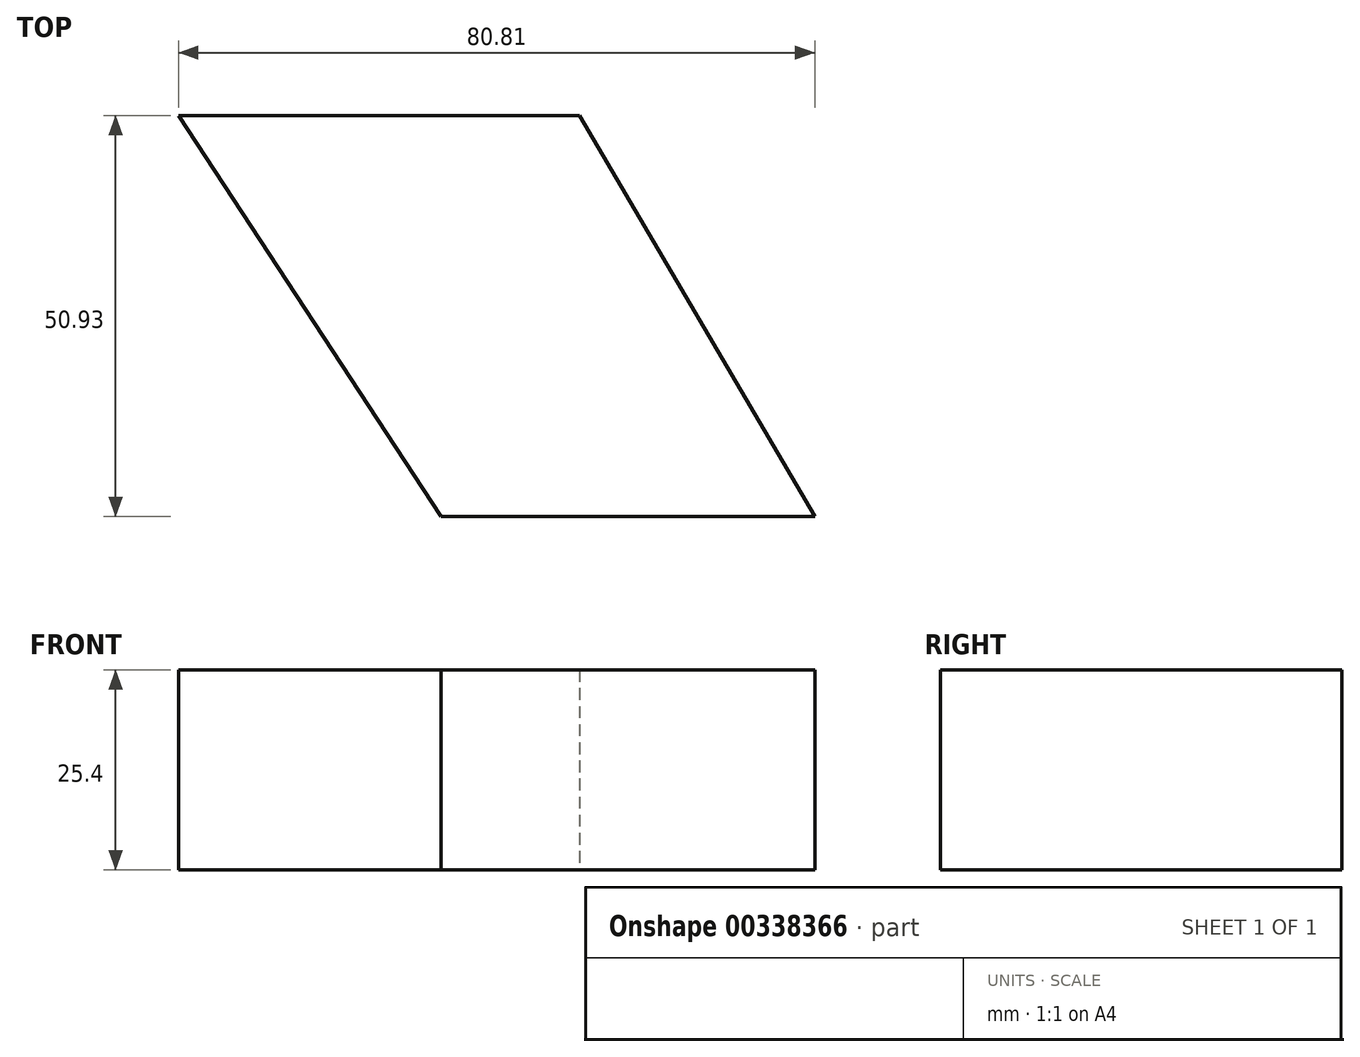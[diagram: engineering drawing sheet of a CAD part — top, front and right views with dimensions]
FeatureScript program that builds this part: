
annotation { "Feature Type Name" : "Feature", "Feature Type Description" : "" }
export const myFeature = defineFeature(function(context is Context, id is Id, definition is map)
    precondition{}
    {
        {
            var Q0;
            Q0=qCreatedBy(makeId("Top.planeOp"),FACE);
            var sketch = newSketch(context, id + "F0", { "sketchPlane" : qUnion([Q0])});
            skLineSegment(sketch, "E0", {"start": v(0, 0) * mm, "end": v(47.46, 0) * mm});
            skLineSegment(sketch, "E1", {"start": v(47.46, 0) * mm, "end": v(17.6, 50.93) * mm});
            skLineSegment(sketch, "E2", {"start": v(17.6, 50.93) * mm, "end": v(-33.35, 50.93) * mm});
            skLineSegment(sketch, "E3", {"start": v(-33.35, 50.93) * mm, "end": v(0, 0) * mm});
            skSolve(sketch);
        }
        {
            var Q0;
            Q0=makeQuery(id+"F0.imprint","IMPRINT",FACE,{"disambiguationData":[TD([[makeQuery(id+"F0.imprint","IMPRINT",EDGE,{"derivedFrom":sQuery(id+"F0.wireOp",EDGE,"E0")}),1.0]])]});
            extrude(context, id + "F1", {"entities" : qUnion([Q0]), "depth" : 25.4 * mm});
        }
    });
